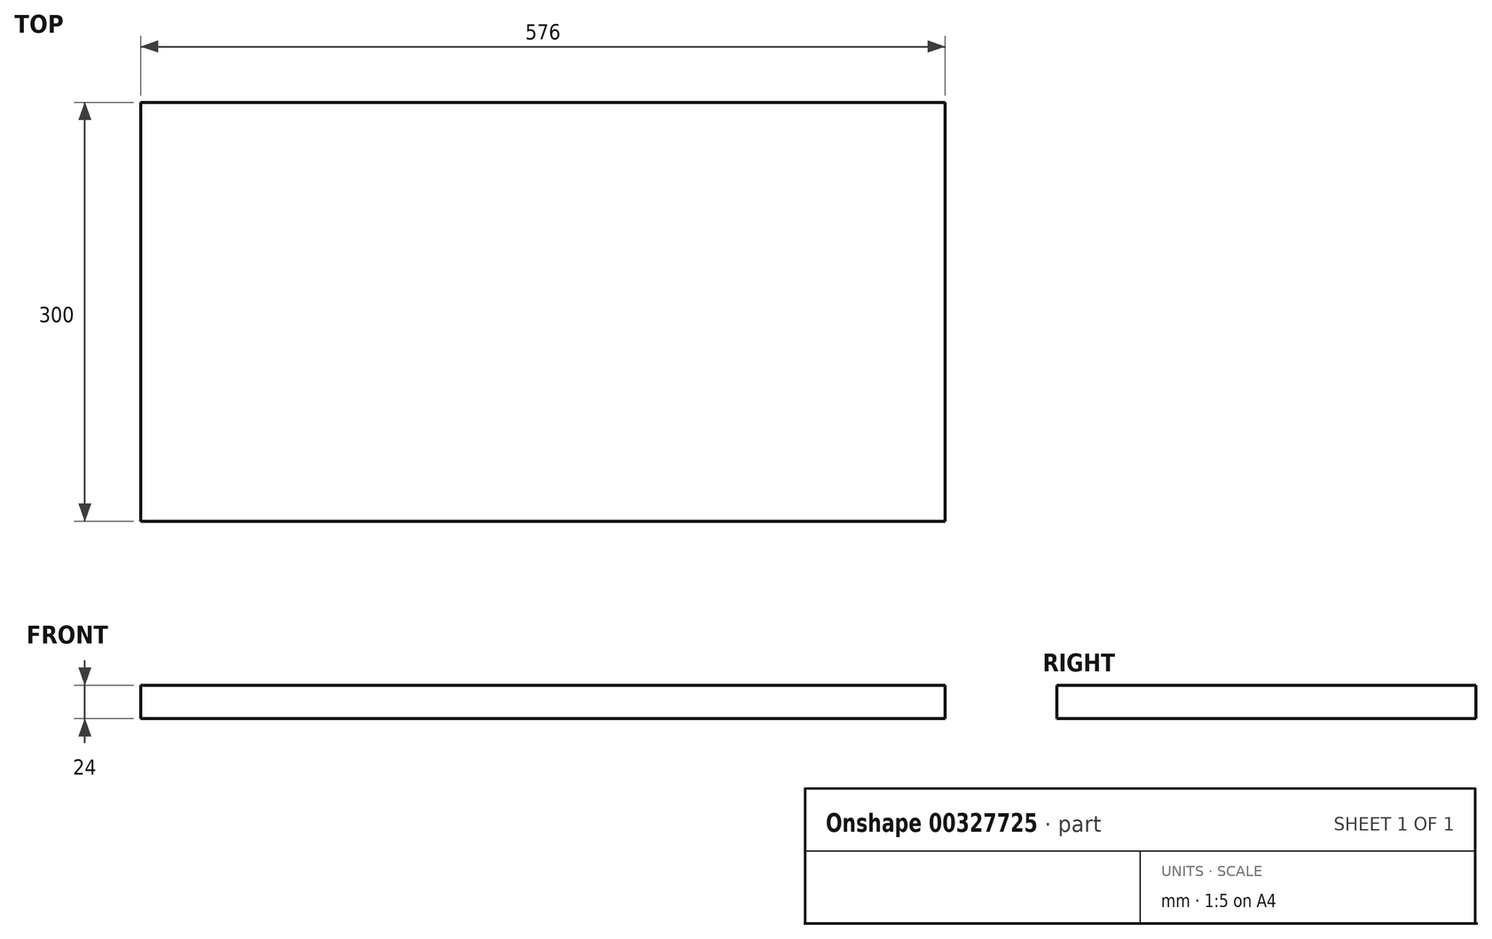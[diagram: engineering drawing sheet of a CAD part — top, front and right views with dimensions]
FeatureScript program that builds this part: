
annotation { "Feature Type Name" : "Feature", "Feature Type Description" : "" }
export const myFeature = defineFeature(function(context is Context, id is Id, definition is map)
    precondition{}
    {
        {
            var Q0;
            Q0=qCreatedBy(makeId("Front.planeOp"),FACE);
            var sketch = newSketch(context, id + "F0", { "sketchPlane" : qUnion([Q0])});
            skLineSegment(sketch, "E0", {"start": v(-58.18, 31.83) * mm, "end": v(-33.18, 31.83) * mm});
            skLineSegment(sketch, "E1", {"start": v(-58.18, 31.83) * mm, "end": v(-346.18, 31.83) * mm});
            skLineSegment(sketch, "E2", {"start": v(-346.18, 31.83) * mm, "end": v(-346.18, 7.83) * mm});
            skLineSegment(sketch, "E3", {"start": v(-346.18, 7.83) * mm, "end": v(-33.18, 7.83) * mm});
            skLineSegment(sketch, "E4", {"start": v(-33.18, 7.83) * mm, "end": v(229.82, 7.83) * mm});
            skLineSegment(sketch, "E5", {"start": v(229.82, 7.83) * mm, "end": v(229.82, 31.83) * mm});
            skLineSegment(sketch, "E6", {"start": v(229.82, 31.83) * mm, "end": v(-33.18, 31.83) * mm});
            skSolve(sketch);
        }
        {
            var Q0;
            Q0=makeQuery(id+"F0.imprint","IMPRINT",FACE,{"disambiguationData":[TD([[makeQuery(id+"F0.imprint","IMPRINT",EDGE,{"derivedFrom":sQuery(id+"F0.wireOp",EDGE,"E0")}),-1.0]])]});
            extrude(context, id + "F1", {"entities" : qUnion([Q0]), "depth" : 300 * mm});
        }
    });
